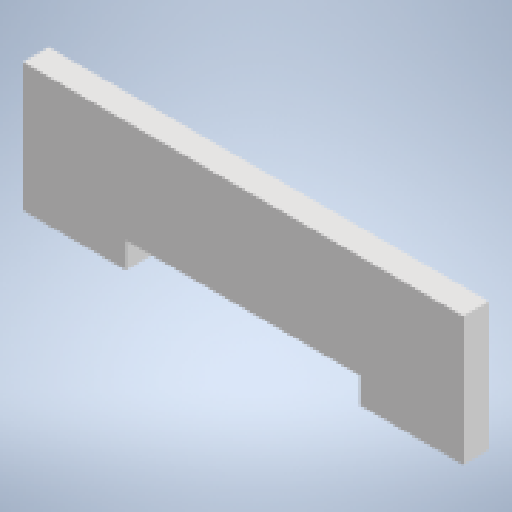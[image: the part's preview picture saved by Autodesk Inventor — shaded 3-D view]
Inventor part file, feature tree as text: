
AUTODESK INVENTOR PART (.ipt)
format: ipt  version: 2024.1 (Build 281209000, 209)  size: 225,792 bytes
history: native  units: mm
features: reference x4, other x3, extrude x3, sketch x3, projected_geometry x1
ambient origin geometry x8: Origin, YZ Plane, XZ Plane, XY Plane, X Axis, Y Axis, Z Axis, Center Point
bodies: Body1 (feature_tree)
feature tree (14):
  other  "ソリッド1"
  extrude  "押し出し1"  Depth=50.0mm
  extrude  "押し出し2"  Depth=10.0mm
  extrude  "押し出し3"  Depth=2.5mm TaperAngle=0.0deg
  sketch  "スケッチ1"
  sketch  "スケッチ2"
  reference  "参照1"
  reference  "参照2"
  projected_geometry  "投影ループ1"
  sketch  "スケッチ3"
  reference  "参照3"
  reference  "参照4"
  other  "Assembly1"
  other  "皿:1"
